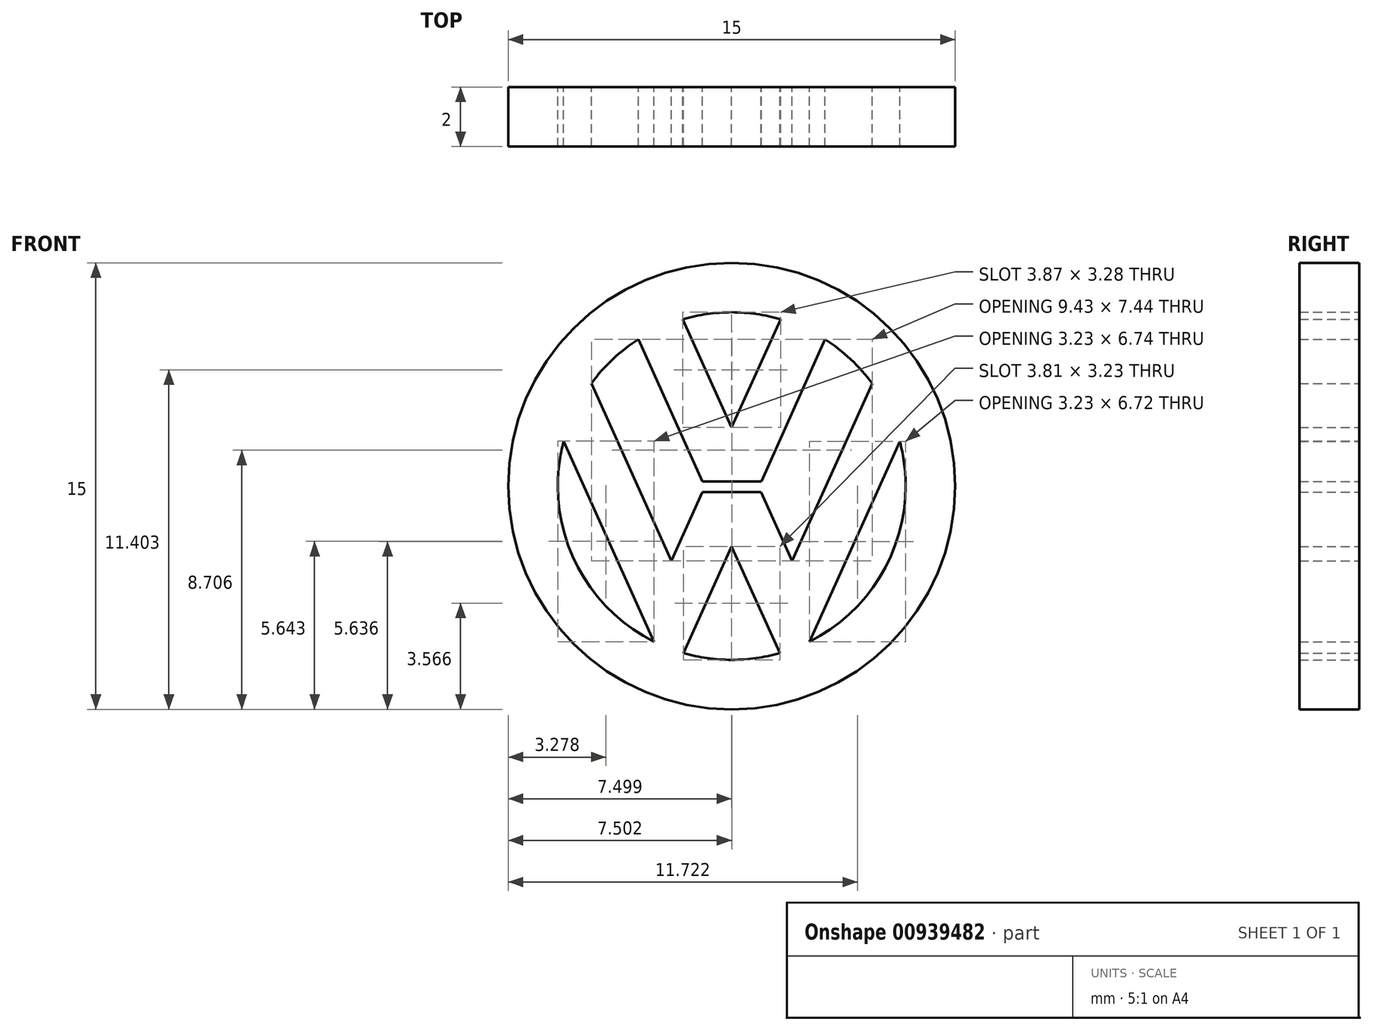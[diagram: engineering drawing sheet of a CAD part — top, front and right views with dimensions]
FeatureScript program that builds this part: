
annotation { "Feature Type Name" : "Feature", "Feature Type Description" : "" }
export const myFeature = defineFeature(function(context is Context, id is Id, definition is map)
    precondition{}
    {
        {
            var Q0;
            Q0=qCreatedBy(makeId("Front.planeOp"),FACE);
            var sketch = newSketch(context, id + "F0", { "sketchPlane" : qUnion([Q0])});
            skArc(sketch, "E0", {"start": v(7.5, 0) * mm, "mid": v(0, 7.5) * mm, "end": v(-7.5, 0) * mm});
            skArc(sketch, "E1", {"start": v(-7.5, 0) * mm, "mid": v(0, -7.5) * mm, "end": v(7.5, 0) * mm});
            skArc(sketch, "E2", {"start": v(2.6, -5.23) * mm, "mid": v(4.96, -3.07) * mm, "end": v(5.84, 0) * mm});
            skArc(sketch, "E3", {"start": v(5.84, 0) * mm, "mid": v(5.79, 0.76) * mm, "end": v(5.64, 1.5) * mm});
            skLineSegment(sketch, "E4", {"start": v(5.64, 1.5) * mm, "end": v(2.6, -5.23) * mm});
            skArc(sketch, "E5", {"start": v(-1.61, -5.61) * mm, "mid": v(-0.82, -5.78) * mm, "end": v(0, -5.84) * mm});
            skArc(sketch, "E6", {"start": v(0, -5.84) * mm, "mid": v(0.81, -5.78) * mm, "end": v(1.61, -5.61) * mm});
            skLineSegment(sketch, "E7", {"start": v(1.61, -5.61) * mm, "end": v(0, -2.03) * mm});
            skLineSegment(sketch, "E8", {"start": v(0, -2.03) * mm, "end": v(-1.61, -5.61) * mm});
            skArc(sketch, "E9", {"start": v(-5.64, 1.51) * mm, "mid": v(-5.79, 0.76) * mm, "end": v(-5.84, 0) * mm});
            skArc(sketch, "E10", {"start": v(-5.84, 0) * mm, "mid": v(-4.96, -3.07) * mm, "end": v(-2.6, -5.23) * mm});
            skLineSegment(sketch, "E11", {"start": v(-2.6, -5.23) * mm, "end": v(-5.64, 1.51) * mm});
            skLineSegment(sketch, "E12", {"start": v(3.13, 4.93) * mm, "end": v(1, 0.16) * mm});
            skLineSegment(sketch, "E13", {"start": v(1, 0.16) * mm, "end": v(-0.98, 0.16) * mm});
            skLineSegment(sketch, "E14", {"start": v(-0.98, 0.16) * mm, "end": v(-3.13, 4.93) * mm});
            skArc(sketch, "E15", {"start": v(-3.13, 4.93) * mm, "mid": v(-4, 4.26) * mm, "end": v(-4.71, 3.45) * mm});
            skLineSegment(sketch, "E16", {"start": v(-4.71, 3.45) * mm, "end": v(-2.02, -2.51) * mm});
            skLineSegment(sketch, "E17", {"start": v(-2.02, -2.51) * mm, "end": v(-0.98, -0.2) * mm});
            skLineSegment(sketch, "E18", {"start": v(-0.98, -0.2) * mm, "end": v(0.98, -0.2) * mm});
            skLineSegment(sketch, "E19", {"start": v(0.98, -0.2) * mm, "end": v(2.02, -2.51) * mm});
            skLineSegment(sketch, "E20", {"start": v(2.02, -2.51) * mm, "end": v(4.72, 3.44) * mm});
            skArc(sketch, "E21", {"start": v(4.72, 3.44) * mm, "mid": v(4, 4.26) * mm, "end": v(3.13, 4.93) * mm});
            skLineSegment(sketch, "E22", {"start": v(-1.64, 5.6) * mm, "end": v(0, 1.97) * mm});
            skLineSegment(sketch, "E23", {"start": v(0, 1.97) * mm, "end": v(1.64, 5.6) * mm});
            skArc(sketch, "E24", {"start": v(1.64, 5.6) * mm, "mid": v(0.83, 5.78) * mm, "end": v(0, 5.84) * mm});
            skArc(sketch, "E25", {"start": v(0, 5.84) * mm, "mid": v(-0.83, 5.78) * mm, "end": v(-1.64, 5.6) * mm});
            skSolve(sketch);
        }
        {
            var Q0;
            Q0 = qSketchRegion(id + "F0", true);
            extrude(context, id + "F1", {"entities" : qUnion([Q0]), "depth" : 2 * mm, "offsetDistance" : 25 * mm});
        }
    });
